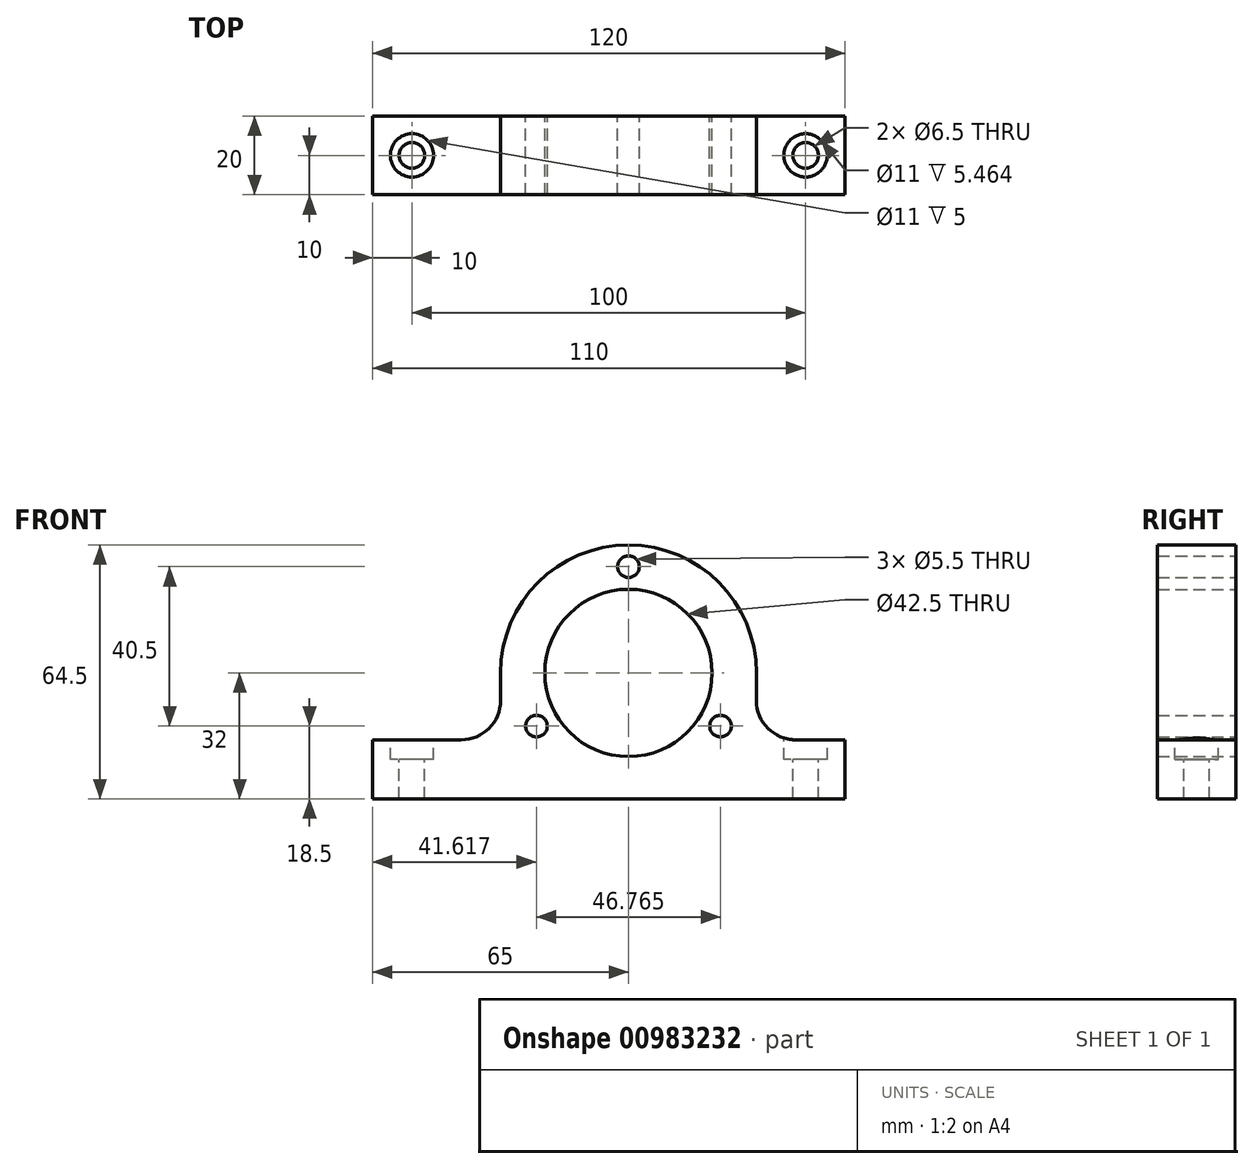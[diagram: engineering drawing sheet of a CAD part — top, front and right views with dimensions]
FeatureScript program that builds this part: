
annotation { "Feature Type Name" : "Feature", "Feature Type Description" : "" }
export const myFeature = defineFeature(function(context is Context, id is Id, definition is map)
    precondition{}
    {
        {
            var Q0;
            Q0=qCreatedBy(makeId("Front.planeOp"),FACE);
            var sketch = newSketch(context, id + "F0", { "sketchPlane" : qUnion([Q0])});
            skCircle(sketch, "E0", {"center": v(0, 0) * mm, "radius": 21.25 * mm});
            skArc(sketch, "E1", {"start": v(32.5, 0) * mm, "mid": v(0, 32.5) * mm, "end": v(-32.5, 0) * mm});
            skCircle(sketch, "E2.cCircle", {"center": v(0, 0) * mm, "radius": 27 * mm, "construction": true});
            skLineSegment(sketch, "E2.0", {"start": v(0, 27) * mm, "end": v(23.38, -13.5) * mm, "construction": true});
            skLineSegment(sketch, "E2.1", {"start": v(23.38, -13.5) * mm, "end": v(-23.38, -13.5) * mm, "construction": true});
            skLineSegment(sketch, "E2.2", {"start": v(-23.38, -13.5) * mm, "end": v(0, 27) * mm, "construction": true});
            skCircle(sketch, "E3", {"center": v(0, 27) * mm, "radius": 2.75 * mm});
            skCircle(sketch, "E4", {"center": v(-23.38, -13.5) * mm, "radius": 2.75 * mm});
            skCircle(sketch, "E5", {"center": v(23.38, -13.5) * mm, "radius": 2.75 * mm});
            skLineSegment(sketch, "E6", {"start": v(-32.5, -32) * mm, "end": v(32.5, -32) * mm});
            skLineSegment(sketch, "E7", {"start": v(-32.5, 0) * mm, "end": v(-32.5, -7) * mm});
            skLineSegment(sketch, "E8", {"start": v(32.5, 0) * mm, "end": v(32.5, -7) * mm});
            skLineSegment(sketch, "E9", {"start": v(-65, -17) * mm, "end": v(-65, -32) * mm});
            skLineSegment(sketch, "E10", {"start": v(55, -17) * mm, "end": v(55, -32) * mm});
            skLineSegment(sketch, "E11", {"start": v(-32.5, -32) * mm, "end": v(-65, -32) * mm});
            skLineSegment(sketch, "E12", {"start": v(32.5, -32) * mm, "end": v(55, -32) * mm});
            skLineSegment(sketch, "E13", {"start": v(-65, -17) * mm, "end": v(-42.5, -17) * mm});
            skLineSegment(sketch, "E14", {"start": v(55, -17) * mm, "end": v(42.5, -17) * mm});
            skPoint(sketch, "E15.visualSharp", {"position": v(-32.5, -17) * mm});
            skArc(sketch, "E15.filletArc", {"start": v(-42.5, -17) * mm, "mid": v(-35.43, -14.07) * mm, "end": v(-32.5, -7) * mm});
            skPoint(sketch, "E16.visualSharp", {"position": v(32.5, -17) * mm});
            skArc(sketch, "E16.filletArc", {"start": v(32.5, -7) * mm, "mid": v(35.43, -14.07) * mm, "end": v(42.5, -17) * mm});
            skSolve(sketch);
        }
        {
            var Q0;
            Q0 = qSketchRegion(id + "F0", true);
            extrude(context, id + "F1", {"entities" : qUnion([Q0]), "depth" : 20 * mm, "offsetDistance" : 25 * mm});
        }
        {
            var Q0;
            Q0=makeQuery(id+"F1.opExtrude","SWEPT_FACE",FACE,{"disambiguationData":[OSD([sQuery(id+"F0.wireOp",EDGE,"E13")])]});
            var sketch = newSketch(context, id + "F2", { "sketchPlane" : qUnion([Q0])});
            skCircle(sketch, "E17", {"center": v(-55, -10) * mm, "radius": 3.25 * mm});
            skCircle(sketch, "E18", {"center": v(45, -10) * mm, "radius": 3.25 * mm});
            skSolve(sketch);
        }
        {
            var Q0;
            Q0 = qSketchRegion(id + "F2", true);
            extrude(context, id + "F3", {"entities" : qUnion([Q0]), "operationType" : NewBodyOperationType.REMOVE, "oppositeDirection" : true, "depth" : 25 * mm, "offsetDistance" : 25 * mm});
        }
        {
            var Q0;
            Q0=qCreatedBy(makeId("Top.planeOp"),FACE);
            var sketch = newSketch(context, id + "F4", { "sketchPlane" : qUnion([Q0])});
            skCircle(sketch, "E19", {"center": v(-55, -10) * mm, "radius": 5.5 * mm});
            skCircle(sketch, "E20", {"center": v(45, -10) * mm, "radius": 5.5 * mm});
            skSolve(sketch);
        }
        {
            var Q0;
            Q0 = qSketchRegion(id + "F4", true);
            extrude(context, id + "F5", {"entities" : qUnion([Q0]), "operationType" : NewBodyOperationType.REMOVE, "oppositeDirection" : true, "depth" : 22 * mm, "offsetDistance" : 25 * mm});
        }
    });
